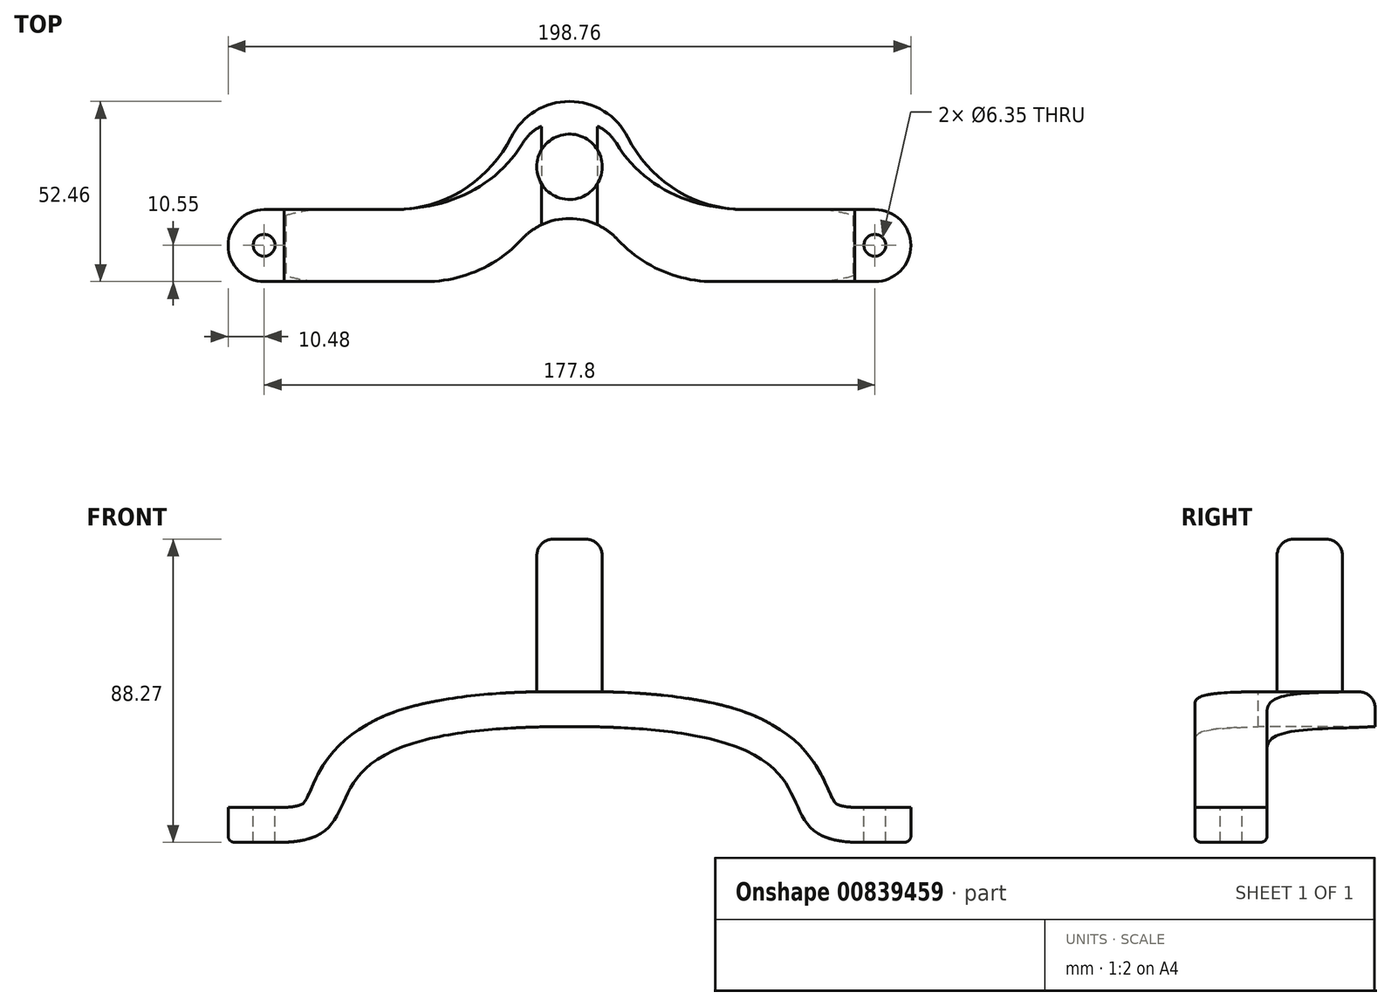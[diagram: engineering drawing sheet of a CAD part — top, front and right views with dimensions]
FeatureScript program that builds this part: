
annotation { "Feature Type Name" : "Feature", "Feature Type Description" : "" }
export const myFeature = defineFeature(function(context is Context, id is Id, definition is map)
    precondition{}
    {
        {
            var Q0;
            Q0=qCreatedBy(makeId("Top.planeOp"),FACE);
            var sketch = newSketch(context, id + "F0", { "sketchPlane" : qUnion([Q0])});
            skCircle(sketch, "E0", {"center": v(0, 0) * mm, "radius": 9.53 * mm});
            skSolve(sketch);
        }
        {
            var Q0;
            Q0=makeQuery(id+"F0.imprint","IMPRINT",FACE,{"disambiguationData":[TD([[makeQuery(id+"F0.imprint","IMPRINT",EDGE,{"derivedFrom":sQuery(id+"F0.wireOp",EDGE,"E0")}),1.0]])]});
            extrude(context, id + "F1", {"entities" : qUnion([Q0]), "depth" : 44.45 * mm, "offsetDistance" : 25.4 * mm});
        }
        {
            var Q0;
            Q0=qCreatedBy(makeId("Top.planeOp"),FACE);
            var sketch = newSketch(context, id + "F2", { "sketchPlane" : qUnion([Q0])});
            skLineSegment(sketch, "E1", {"start": v(0, 0) * mm, "end": v(0, -22.86) * mm, "construction": true});
            skLineSegment(sketch, "E2", {"start": v(0, -22.86) * mm, "end": v(88.9, -22.86) * mm, "construction": true});
            skLineSegment(sketch, "E3", {"start": v(0, -22.86) * mm, "end": v(-88.9, -22.86) * mm, "construction": true});
            skCircle(sketch, "E4", {"center": v(-88.9, -22.86) * mm, "radius": 3.18 * mm});
            skCircle(sketch, "E5", {"center": v(88.9, -22.86) * mm, "radius": 3.18 * mm});
            skSolve(sketch);
        }
        {
            var Q0;
            Q0=qCreatedBy(makeId("Top.planeOp"),FACE);
            var sketch = newSketch(context, id + "F3", { "sketchPlane" : qUnion([Q0])});
            skArc(sketch, "E6", {"start": v(14.41, -12.46) * mm, "mid": v(0, 19.05) * mm, "end": v(-14.41, -12.46) * mm});
            skLineSegment(sketch, "E7.bottom", {"start": v(88.9, -33.41) * mm, "end": v(-88.9, -33.41) * mm});
            skLineSegment(sketch, "E7.top", {"start": v(88.9, -12.46) * mm, "end": v(14.41, -12.46) * mm});
            skLineSegment(sketch, "E7.left", {"start": v(88.9, -33.41) * mm, "end": v(88.9, -12.46) * mm});
            skLineSegment(sketch, "E7.right", {"start": v(-88.9, -33.41) * mm, "end": v(-88.9, -12.46) * mm});
            skPoint(sketch, "E7.middle", {"position": v(0, -22.94) * mm});
            skLineSegment(sketch, "E8.trimOffspring", {"start": v(-14.41, -12.46) * mm, "end": v(-88.9, -12.46) * mm});
            skLineSegment(sketch, "E9", {"start": v(0, 0) * mm, "end": v(0, -22.94) * mm, "construction": true});
            skLineSegment(sketch, "E10", {"start": v(0, -22.94) * mm, "end": v(-88.9, -22.94) * mm, "construction": true});
            skLineSegment(sketch, "E11", {"start": v(0, -22.94) * mm, "end": v(88.9, -22.94) * mm, "construction": true});
            skCircle(sketch, "E12", {"center": v(-88.9, -22.94) * mm, "radius": 10.48 * mm});
            skCircle(sketch, "E13", {"center": v(88.9, -22.94) * mm, "radius": 10.48 * mm});
            skSolve(sketch);
        }
        {
            var Q0;
            Q0=makeQuery(id+"F3.imprint","IMPRINT",FACE,{"disambiguationData":[TD([[makeQuery(id+"F3.imprint","IMPRINT",EDGE,{"derivedFrom":sQuery(id+"F3.wireOp",EDGE,"E6")}),1.0]])]});
            var Q1;
            {var subQ0=sQuery(id+"F3.wireOp",EDGE,"E7.right");Q1=makeQuery(id+"F3.imprint","IMPRINT",FACE,{"disambiguationData":[TD([[makeQuery(id+"F3.imprint","IMPRINT",EDGE,{"derivedFrom":subQ0}),-1.0]])]});}
            var Q2;
            {var subQ0=sQuery(id+"F3.wireOp",EDGE,"E7.right");Q2=makeQuery(id+"F3.imprint","IMPRINT",FACE,{"disambiguationData":[TD([[makeQuery(id+"F3.imprint","IMPRINT",EDGE,{"derivedFrom":subQ0}),1.0]])]});}
            var Q3;
            {var subQ0=sQuery(id+"F3.wireOp",EDGE,"E7.left");Q3=makeQuery(id+"F3.imprint","IMPRINT",FACE,{"disambiguationData":[TD([[makeQuery(id+"F3.imprint","IMPRINT",EDGE,{"derivedFrom":subQ0}),1.0]])]});}
            var Q4;
            {var subQ0=sQuery(id+"F3.wireOp",EDGE,"E7.left");Q4=makeQuery(id+"F3.imprint","IMPRINT",FACE,{"disambiguationData":[TD([[makeQuery(id+"F3.imprint","IMPRINT",EDGE,{"derivedFrom":subQ0}),-1.0]])]});}
            extrude(context, id + "F4", {"entities" : qUnion([Q0, Q1, Q2, Q3, Q4]), "operationType" : NewBodyOperationType.ADD, "oppositeDirection" : true, "depth" : 43.81 * mm, "offsetDistance" : 25.4 * mm});
        }
        {
            var Q0;
            Q0=makeQuery(id+"F4.opExtrude","SWEPT_EDGE",EDGE,{"disambiguationData":[OSD([sQuery(id+"F3.wireOp",EDGE,"E6"),sQuery(id+"F3.wireOp",EDGE,"E7.top")])]});
            var Q1;
            Q1=makeQuery(id+"F4.opExtrude","SWEPT_EDGE",EDGE,{"disambiguationData":[OSD([sQuery(id+"F3.wireOp",EDGE,"E6"),sQuery(id+"F3.wireOp",EDGE,"E8.trimOffspring")])]});
            fillet(context, id + "F5", {"entities" : qUnion([Q0, Q1]), "radius" : 38.1 * mm, "tangentPropagation" : true, "allowEdgeOverflow" : false});
        }
        {
            var Q0;
            Q0=makeQuery(id+"F4.opExtrude","SWEPT_FACE",FACE,{"disambiguationData":[OSD([sQuery(id+"F3.wireOp",EDGE,"E7.bottom")])]});
            var sketch = newSketch(context, id + "F6", { "sketchPlane" : qUnion([Q0])});
            skLineSegment(sketch, "E14", {"start": v(0, -43.81) * mm, "end": v(-82.55, -43.82) * mm, "construction": true});
            skLineSegment(sketch, "E15", {"start": v(-83.03, -33.67) * mm, "end": v(-104.9, -33.67) * mm});
            skLineSegment(sketch, "E16", {"start": v(-104.9, -33.67) * mm, "end": v(-104.9, -43.82) * mm});
            skLineSegment(sketch, "E17", {"start": v(-104.9, -43.82) * mm, "end": v(-82.55, -43.82) * mm});
            skLineSegment(sketch, "E18", {"start": v(83.03, -33.67) * mm, "end": v(108.35, -33.67) * mm});
            skLineSegment(sketch, "E19", {"start": v(108.35, -33.67) * mm, "end": v(108.35, -43.82) * mm});
            skLineSegment(sketch, "E20", {"start": v(108.35, -43.82) * mm, "end": v(82.55, -43.82) * mm});
            skLineSegment(sketch, "E21", {"start": v(0, 0) * mm, "end": v(0, -10.16) * mm, "construction": true});
            skFitSpline(sketch, "E22", {"points": [v(-82.55, -43.82) * mm, v(0, -10.16) * mm], "startDerivative": vector(94.97, 4.46) * mm, "endDerivative": vector(266.7, -0.76) * mm});
            skFitSpline(sketch, "E23.MirrorCS", {"points": [v(82.55, -43.82) * mm, v(0, -10.16) * mm], "startDerivative": vector(-94.97, 4.46) * mm, "endDerivative": vector(-266.7, -0.76) * mm});
            skFitSpline(sketch, "E24.0", {"points": [v(-83.03, -33.67) * mm, v(-82.27, -33.63) * mm, v(-80.92, -33.52) * mm, v(-79.44, -33.26) * mm, v(-78.44, -32.98) * mm, v(-77.87, -32.74) * mm, v(-77.6, -32.58) * mm, v(-77.47, -32.48) * mm, v(-77.35, -32.36) * mm, v(-77.13, -32.1) * mm, v(-76.8, -31.6) * mm, v(-76.38, -30.8) * mm, v(-75.87, -29.71) * mm, v(-75.05, -27.88) * mm, v(-73.73, -24.94) * mm, v(-71.75, -21.4) * mm, v(-69.6, -18.44) * mm, v(-67.66, -16.22) * mm, v(-65.4, -14.07) * mm, v(-62.81, -12.02) * mm, v(-59.9, -10.12) * mm, v(-55.57, -7.8) * mm, v(-49.32, -5.32) * mm, v(-40.25, -2.98) * mm, v(-29.3, -1.27) * mm, v(-16.15, -0.21) * mm, v(-5.68, 0.02) * mm, v(0.03, 0) * mm]});
            skFitSpline(sketch, "E25.0", {"points": [v(83.03, -33.67) * mm, v(82.27, -33.63) * mm, v(80.92, -33.52) * mm, v(79.44, -33.26) * mm, v(78.44, -32.98) * mm, v(77.87, -32.74) * mm, v(77.6, -32.58) * mm, v(77.47, -32.48) * mm, v(77.35, -32.36) * mm, v(77.13, -32.1) * mm, v(76.8, -31.6) * mm, v(76.38, -30.8) * mm, v(75.87, -29.71) * mm, v(75.05, -27.88) * mm, v(73.73, -24.94) * mm, v(71.75, -21.4) * mm, v(69.6, -18.44) * mm, v(67.66, -16.22) * mm, v(65.4, -14.07) * mm, v(62.81, -12.02) * mm, v(59.9, -10.12) * mm, v(55.57, -7.8) * mm, v(49.32, -5.32) * mm, v(40.25, -2.98) * mm, v(29.3, -1.27) * mm, v(16.15, -0.21) * mm, v(5.68, 0.02) * mm, v(-0.03, 0) * mm]});
            skSolve(sketch);
        }
        {
            var Q0;
            Q0 = qSketchRegion(id + "F6", true);
            extrude(context, id + "F7", {"entities" : qUnion([Q0]), "operationType" : NewBodyOperationType.INTERSECT, "endBound" : BoundingType.THROUGH_ALL, "oppositeDirection" : true, "depth" : 25.4 * mm, "offsetDistance" : 25.4 * mm});
        }
        {
            var Q0;
            Q0 = qSketchRegion(id + "F0", true);
            extrude(context, id + "F8", {"entities" : qUnion([Q0]), "operationType" : NewBodyOperationType.ADD, "depth" : 44.45 * mm, "offsetDistance" : 25.4 * mm});
        }
        {
            var Q0;
            {var subQ0=sQuery(id+"F3.wireOp",EDGE,"E7.bottom");Q0=makeQuery(id+"F7.boolean.opBoolean","SPLIT",FACE,{"disambiguationData":[TD([makeQuery(id+"F4.opExtrude","SWEPT_FACE",FACE,{"disambiguationData":[OSD([subQ0])]})])],"derivedFrom":makeQuery(id+"F4.opExtrude","CAP_FACE",FACE,{"disambiguationData":[OSD([sQuery(id+"F3.wireOp",EDGE,"E6"),subQ0,sQuery(id+"F3.wireOp",EDGE,"E7.top"),sQuery(id+"F3.wireOp",EDGE,"E8.trimOffspring"),sQuery(id+"F3.wireOp",EDGE,"E12"),sQuery(id+"F3.wireOp",EDGE,"E13")])],"isStart":true})});}
            var sketch = newSketch(context, id + "F9", { "sketchPlane" : qUnion([Q0])});
            skCircle(sketch, "E26", {"center": v(0, -34.1) * mm, "radius": 19.05 * mm});
            skSolve(sketch);
        }
        {
            var Q0;
            {var subQ1=sQuery(id+"F3.wireOp",EDGE,"E7.bottom");var subQ7=makeQuery(id+"F4.opExtrude","CAP_EDGE",EDGE,{"disambiguationData":[OSD([subQ1])],"isStart":true});Q0=makeQuery(id+"F9.imprint","IMPRINT",FACE,{"disambiguationData":[TD([[makeQuery(id+"F9.imprint","IMPRINT",EDGE,{"derivedFrom":subQ7}),-1.0]])]});}
            var Q1;
            {var subQ1=sQuery(id+"F3.wireOp",EDGE,"E7.bottom");var subQ7=makeQuery(id+"F4.opExtrude","CAP_EDGE",EDGE,{"disambiguationData":[OSD([subQ1])],"isStart":true});Q1=makeQuery(id+"F9.imprint","IMPRINT",FACE,{"disambiguationData":[TD([[makeQuery(id+"F9.imprint","IMPRINT",EDGE,{"derivedFrom":subQ7}),1.0]])]});}
            extrude(context, id + "F10", {"entities" : qUnion([Q0, Q1]), "operationType" : NewBodyOperationType.REMOVE, "endBound" : BoundingType.THROUGH_ALL, "oppositeDirection" : true, "depth" : 25.4 * mm, "offsetDistance" : 25.4 * mm});
        }
        {
            var Q0;
            Q0=makeQuery(id+"F10.boolean.opBoolean","INTERSECT",EDGE,{"disambiguationData":[OD(0.0)],"derivedFrom":[makeQuery(id+"F4.opExtrude","SWEPT_FACE",FACE,{"disambiguationData":[OSD([sQuery(id+"F3.wireOp",EDGE,"E7.bottom")])]}),makeQuery(id+"F10.opExtrude","SWEPT_FACE",FACE,{"disambiguationData":[OSD([sQuery(id+"F9.wireOp",EDGE,"E26")])]})]});
            var Q1;
            Q1=makeQuery(id+"F10.boolean.opBoolean","INTERSECT",EDGE,{"disambiguationData":[OD(1.0)],"derivedFrom":[makeQuery(id+"F4.opExtrude","SWEPT_FACE",FACE,{"disambiguationData":[OSD([sQuery(id+"F3.wireOp",EDGE,"E7.bottom")])]}),makeQuery(id+"F10.opExtrude","SWEPT_FACE",FACE,{"disambiguationData":[OSD([sQuery(id+"F9.wireOp",EDGE,"E26")])]})]});
            fillet(context, id + "F11", {"entities" : qUnion([Q0, Q1]), "radius" : 38.1 * mm, "tangentPropagation" : true, "allowEdgeOverflow" : false});
        }
        {
            var Q0;
            Q0=makeQuery(id+"F4.opExtrude","CAP_EDGE",EDGE,{"disambiguationData":[OSD([sQuery(id+"F3.wireOp",EDGE,"E6")])],"isStart":true});
            var Q1;
            Q1=makeQuery(id+"F7.boolean.opBoolean","INTERSECT",EDGE,{"derivedFrom":[makeQuery(id+"F4.opExtrude","SWEPT_FACE",FACE,{"disambiguationData":[OSD([sQuery(id+"F3.wireOp",EDGE,"E6")])]}),makeQuery(id+"F7.boolean.toolComplement.opBoolean","COPY",FACE,{"derivedFrom":makeQuery(id+"F7.opExtrude","SWEPT_FACE",FACE,{"disambiguationData":[OSD([sQuery(id+"F6.wireOp",EDGE,"a3f56aa1-5c8b-43e5-82c6-7868b8ca9d38.0")])]})})]});
            var Q2;
            Q2=makeQuery(id+"F7.boolean.opBoolean","INTERSECT",EDGE,{"derivedFrom":[makeQuery(id+"F5.opFillet","BLEND_FACE",FACE,{"disambiguationData":[OSD([sQuery(id+"F3.wireOp",EDGE,"E6"),sQuery(id+"F3.wireOp",EDGE,"E7.top")])]}),makeQuery(id+"F7.boolean.toolComplement.opBoolean","COPY",FACE,{"derivedFrom":makeQuery(id+"F7.opExtrude","SWEPT_FACE",FACE,{"disambiguationData":[OSD([sQuery(id+"F6.wireOp",EDGE,"2b992f9c-3d7e-4ba6-b69b-49b9b1f304800.MirrorCS")])]})})]});
            var Q3;
            Q3=makeQuery(id+"F7.boolean.opBoolean","INTERSECT",EDGE,{"derivedFrom":[makeQuery(id+"F4.opExtrude","SWEPT_FACE",FACE,{"disambiguationData":[OSD([sQuery(id+"F3.wireOp",EDGE,"E6")])]}),makeQuery(id+"F7.boolean.toolComplement.opBoolean","COPY",FACE,{"derivedFrom":makeQuery(id+"F7.opExtrude","SWEPT_FACE",FACE,{"disambiguationData":[OSD([sQuery(id+"F6.wireOp",EDGE,"2b992f9c-3d7e-4ba6-b69b-49b9b1f304800.MirrorCS")])]})})]});
            var Q4;
            Q4=makeQuery(id+"F7.boolean.opBoolean","INTERSECT",EDGE,{"derivedFrom":[makeQuery(id+"F4.opExtrude","SWEPT_FACE",FACE,{"disambiguationData":[OSD([sQuery(id+"F3.wireOp",EDGE,"E6")])]}),makeQuery(id+"F7.boolean.toolComplement.opBoolean","COPY",FACE,{"derivedFrom":makeQuery(id+"F7.opExtrude","SWEPT_FACE",FACE,{"disambiguationData":[OSD([sQuery(id+"F6.wireOp",EDGE,"f722ad29-e965-4c17-baed-5adea42b7f95")])]})})]});
            var Q5;
            Q5=makeQuery(id+"F7.boolean.opBoolean","INTERSECT",EDGE,{"derivedFrom":[makeQuery(id+"F5.opFillet","BLEND_FACE",FACE,{"disambiguationData":[OSD([sQuery(id+"F3.wireOp",EDGE,"E6"),sQuery(id+"F3.wireOp",EDGE,"E8.trimOffspring")])]}),makeQuery(id+"F7.boolean.toolComplement.opBoolean","COPY",FACE,{"derivedFrom":makeQuery(id+"F7.opExtrude","SWEPT_FACE",FACE,{"disambiguationData":[OSD([sQuery(id+"F6.wireOp",EDGE,"f722ad29-e965-4c17-baed-5adea42b7f95")])]})})]});
            var Q6;
            Q6=makeQuery(id+"F7.boolean.opBoolean","INTERSECT",EDGE,{"derivedFrom":[makeQuery(id+"F4.opExtrude","SWEPT_FACE",FACE,{"disambiguationData":[OSD([sQuery(id+"F3.wireOp",EDGE,"E8.trimOffspring")])]}),makeQuery(id+"F7.boolean.toolComplement.opBoolean","COPY",FACE,{"derivedFrom":makeQuery(id+"F7.opExtrude","SWEPT_FACE",FACE,{"disambiguationData":[OSD([sQuery(id+"F6.wireOp",EDGE,"f722ad29-e965-4c17-baed-5adea42b7f95")])]})})]});
            var Q7;
            Q7=makeQuery(id+"F7.boolean.opBoolean","INTERSECT",EDGE,{"derivedFrom":[makeQuery(id+"F4.opExtrude","SWEPT_FACE",FACE,{"disambiguationData":[OSD([sQuery(id+"F3.wireOp",EDGE,"E8.trimOffspring")])]}),makeQuery(id+"F7.boolean.toolComplement.opBoolean","COPY",FACE,{"derivedFrom":makeQuery(id+"F7.opExtrude","SWEPT_FACE",FACE,{"disambiguationData":[OSD([sQuery(id+"F6.wireOp",EDGE,"0e30f15a-034d-4650-8b6f-ae2eca744b7f.0")])]})})]});
            var Q8;
            Q8=makeQuery(id+"F7.boolean.opBoolean","INTERSECT",EDGE,{"derivedFrom":[makeQuery(id+"F5.opFillet","BLEND_FACE",FACE,{"disambiguationData":[OSD([sQuery(id+"F3.wireOp",EDGE,"E6"),sQuery(id+"F3.wireOp",EDGE,"E8.trimOffspring")])]}),makeQuery(id+"F7.boolean.toolComplement.opBoolean","COPY",FACE,{"derivedFrom":makeQuery(id+"F7.opExtrude","SWEPT_FACE",FACE,{"disambiguationData":[OSD([sQuery(id+"F6.wireOp",EDGE,"0e30f15a-034d-4650-8b6f-ae2eca744b7f.0")])]})})]});
            var Q9;
            Q9=makeQuery(id+"F7.boolean.opBoolean","INTERSECT",EDGE,{"derivedFrom":[makeQuery(id+"F4.opExtrude","SWEPT_FACE",FACE,{"disambiguationData":[OSD([sQuery(id+"F3.wireOp",EDGE,"E6")])]}),makeQuery(id+"F7.boolean.toolComplement.opBoolean","COPY",FACE,{"derivedFrom":makeQuery(id+"F7.opExtrude","SWEPT_FACE",FACE,{"disambiguationData":[OSD([sQuery(id+"F6.wireOp",EDGE,"0e30f15a-034d-4650-8b6f-ae2eca744b7f.0")])]})})]});
            var Q10;
            Q10=makeQuery(id+"F7.boolean.opBoolean","INTERSECT",EDGE,{"derivedFrom":[makeQuery(id+"F5.opFillet","BLEND_FACE",FACE,{"disambiguationData":[OSD([sQuery(id+"F3.wireOp",EDGE,"E6"),sQuery(id+"F3.wireOp",EDGE,"E7.top")])]}),makeQuery(id+"F7.boolean.toolComplement.opBoolean","COPY",FACE,{"derivedFrom":makeQuery(id+"F7.opExtrude","SWEPT_FACE",FACE,{"disambiguationData":[OSD([sQuery(id+"F6.wireOp",EDGE,"a3f56aa1-5c8b-43e5-82c6-7868b8ca9d38.0")])]})})]});
            var Q11;
            Q11=makeQuery(id+"F7.boolean.opBoolean","INTERSECT",EDGE,{"derivedFrom":[makeQuery(id+"F4.opExtrude","SWEPT_FACE",FACE,{"disambiguationData":[OSD([sQuery(id+"F3.wireOp",EDGE,"E7.top")])]}),makeQuery(id+"F7.boolean.toolComplement.opBoolean","COPY",FACE,{"derivedFrom":makeQuery(id+"F7.opExtrude","SWEPT_FACE",FACE,{"disambiguationData":[OSD([sQuery(id+"F6.wireOp",EDGE,"2b992f9c-3d7e-4ba6-b69b-49b9b1f304800.MirrorCS")])]})})]});
            var Q12;
            Q12=makeQuery(id+"F7.boolean.opBoolean","COPY",EDGE,{"derivedFrom":makeQuery(id+"F7.boolean.toolComplement.opBoolean","COPY",EDGE,{"derivedFrom":makeQuery(id+"F7.opExtrude","CAP_EDGE",EDGE,{"disambiguationData":[OSD([sQuery(id+"F6.wireOp",EDGE,"0e30f15a-034d-4650-8b6f-ae2eca744b7f.0")])],"isStart":true})})});
            var Q13;
            Q13=makeQuery(id+"F11.opFillet","BLEND_EDGE",EDGE,{"blendedFrom":[makeQuery(id+"F10.boolean.opBoolean","INTERSECT",EDGE,{"disambiguationData":[OD(0.0)],"derivedFrom":[makeQuery(id+"F4.opExtrude","SWEPT_FACE",FACE,{"disambiguationData":[OSD([sQuery(id+"F3.wireOp",EDGE,"E7.bottom")])]}),makeQuery(id+"F10.opExtrude","SWEPT_FACE",FACE,{"disambiguationData":[OSD([sQuery(id+"F9.wireOp",EDGE,"E26")])]})]}),makeQuery(id+"F7.boolean.opBoolean","COPY",FACE,{"derivedFrom":makeQuery(id+"F7.boolean.toolComplement.opBoolean","COPY",FACE,{"derivedFrom":makeQuery(id+"F7.opExtrude","SWEPT_FACE",FACE,{"disambiguationData":[OSD([sQuery(id+"F6.wireOp",EDGE,"0e30f15a-034d-4650-8b6f-ae2eca744b7f.0")])]})})})],"blendedInto":[makeQuery(id+"F7.boolean.opBoolean","COPY",FACE,{"derivedFrom":makeQuery(id+"F7.boolean.toolComplement.opBoolean","COPY",FACE,{"derivedFrom":makeQuery(id+"F7.opExtrude","SWEPT_FACE",FACE,{"disambiguationData":[OSD([sQuery(id+"F6.wireOp",EDGE,"0e30f15a-034d-4650-8b6f-ae2eca744b7f.0")])]})})})]});
            var Q14;
            Q14=makeQuery(id+"F11.opFillet","BLEND_EDGE",EDGE,{"blendedFrom":[makeQuery(id+"F10.boolean.opBoolean","INTERSECT",EDGE,{"disambiguationData":[OD(0.0)],"derivedFrom":[makeQuery(id+"F4.opExtrude","SWEPT_FACE",FACE,{"disambiguationData":[OSD([sQuery(id+"F3.wireOp",EDGE,"E7.bottom")])]}),makeQuery(id+"F10.opExtrude","SWEPT_FACE",FACE,{"disambiguationData":[OSD([sQuery(id+"F9.wireOp",EDGE,"E26")])]})]}),makeQuery(id+"F7.boolean.opBoolean","COPY",FACE,{"derivedFrom":makeQuery(id+"F7.boolean.toolComplement.opBoolean","COPY",FACE,{"derivedFrom":makeQuery(id+"F7.opExtrude","SWEPT_FACE",FACE,{"disambiguationData":[OSD([sQuery(id+"F6.wireOp",EDGE,"f722ad29-e965-4c17-baed-5adea42b7f95")])]})})})],"blendedInto":[makeQuery(id+"F7.boolean.opBoolean","COPY",FACE,{"derivedFrom":makeQuery(id+"F7.boolean.toolComplement.opBoolean","COPY",FACE,{"derivedFrom":makeQuery(id+"F7.opExtrude","SWEPT_FACE",FACE,{"disambiguationData":[OSD([sQuery(id+"F6.wireOp",EDGE,"f722ad29-e965-4c17-baed-5adea42b7f95")])]})})})]});
            var Q15;
            Q15=makeQuery(id+"F7.boolean.opBoolean","COPY",EDGE,{"derivedFrom":makeQuery(id+"F7.boolean.toolComplement.opBoolean","COPY",EDGE,{"derivedFrom":makeQuery(id+"F7.opExtrude","CAP_EDGE",EDGE,{"disambiguationData":[OSD([sQuery(id+"F6.wireOp",EDGE,"f722ad29-e965-4c17-baed-5adea42b7f95")])],"isStart":true})})});
            var Q16;
            Q16=makeQuery(id+"F10.boolean.opBoolean","INTERSECT",EDGE,{"derivedFrom":[makeQuery(id+"F7.boolean.opBoolean","COPY",FACE,{"derivedFrom":makeQuery(id+"F7.boolean.toolComplement.opBoolean","COPY",FACE,{"derivedFrom":makeQuery(id+"F7.opExtrude","SWEPT_FACE",FACE,{"disambiguationData":[OSD([sQuery(id+"F6.wireOp",EDGE,"0e30f15a-034d-4650-8b6f-ae2eca744b7f.0")])]})})}),makeQuery(id+"F10.opExtrude","SWEPT_FACE",FACE,{"disambiguationData":[OSD([sQuery(id+"F9.wireOp",EDGE,"E26")])]})]});
            var Q17;
            Q17=makeQuery(id+"F10.boolean.opBoolean","COPY",EDGE,{"derivedFrom":makeQuery(id+"F10.opExtrude","CAP_EDGE",EDGE,{"disambiguationData":[OSD([sQuery(id+"F9.wireOp",EDGE,"E26")])],"isStart":true})});
            var Q18;
            Q18=makeQuery(id+"F10.boolean.opBoolean","INTERSECT",EDGE,{"derivedFrom":[makeQuery(id+"F7.boolean.opBoolean","COPY",FACE,{"derivedFrom":makeQuery(id+"F7.boolean.toolComplement.opBoolean","COPY",FACE,{"derivedFrom":makeQuery(id+"F7.opExtrude","SWEPT_FACE",FACE,{"disambiguationData":[OSD([sQuery(id+"F6.wireOp",EDGE,"f722ad29-e965-4c17-baed-5adea42b7f95")])]})})}),makeQuery(id+"F10.opExtrude","SWEPT_FACE",FACE,{"disambiguationData":[OSD([sQuery(id+"F9.wireOp",EDGE,"E26")])]})]});
            var Q19;
            Q19=makeQuery(id+"F11.opFillet","BLEND_EDGE",EDGE,{"blendedFrom":[makeQuery(id+"F10.boolean.opBoolean","INTERSECT",EDGE,{"disambiguationData":[OD(1.0)],"derivedFrom":[makeQuery(id+"F4.opExtrude","SWEPT_FACE",FACE,{"disambiguationData":[OSD([sQuery(id+"F3.wireOp",EDGE,"E7.bottom")])]}),makeQuery(id+"F10.opExtrude","SWEPT_FACE",FACE,{"disambiguationData":[OSD([sQuery(id+"F9.wireOp",EDGE,"E26")])]})]}),makeQuery(id+"F7.boolean.opBoolean","COPY",FACE,{"derivedFrom":makeQuery(id+"F7.boolean.toolComplement.opBoolean","COPY",FACE,{"derivedFrom":makeQuery(id+"F7.opExtrude","SWEPT_FACE",FACE,{"disambiguationData":[OSD([sQuery(id+"F6.wireOp",EDGE,"a3f56aa1-5c8b-43e5-82c6-7868b8ca9d38.0")])]})})})],"blendedInto":[makeQuery(id+"F7.boolean.opBoolean","COPY",FACE,{"derivedFrom":makeQuery(id+"F7.boolean.toolComplement.opBoolean","COPY",FACE,{"derivedFrom":makeQuery(id+"F7.opExtrude","SWEPT_FACE",FACE,{"disambiguationData":[OSD([sQuery(id+"F6.wireOp",EDGE,"a3f56aa1-5c8b-43e5-82c6-7868b8ca9d38.0")])]})})})]});
            var Q20;
            Q20=makeQuery(id+"F11.opFillet","BLEND_EDGE",EDGE,{"blendedFrom":[makeQuery(id+"F10.boolean.opBoolean","INTERSECT",EDGE,{"disambiguationData":[OD(1.0)],"derivedFrom":[makeQuery(id+"F4.opExtrude","SWEPT_FACE",FACE,{"disambiguationData":[OSD([sQuery(id+"F3.wireOp",EDGE,"E7.bottom")])]}),makeQuery(id+"F10.opExtrude","SWEPT_FACE",FACE,{"disambiguationData":[OSD([sQuery(id+"F9.wireOp",EDGE,"E26")])]})]}),makeQuery(id+"F7.boolean.opBoolean","COPY",FACE,{"derivedFrom":makeQuery(id+"F7.boolean.toolComplement.opBoolean","COPY",FACE,{"derivedFrom":makeQuery(id+"F7.opExtrude","SWEPT_FACE",FACE,{"disambiguationData":[OSD([sQuery(id+"F6.wireOp",EDGE,"2b992f9c-3d7e-4ba6-b69b-49b9b1f304800.MirrorCS")])]})})})],"blendedInto":[makeQuery(id+"F7.boolean.opBoolean","COPY",FACE,{"derivedFrom":makeQuery(id+"F7.boolean.toolComplement.opBoolean","COPY",FACE,{"derivedFrom":makeQuery(id+"F7.opExtrude","SWEPT_FACE",FACE,{"disambiguationData":[OSD([sQuery(id+"F6.wireOp",EDGE,"2b992f9c-3d7e-4ba6-b69b-49b9b1f304800.MirrorCS")])]})})})]});
            var Q21;
            Q21=makeQuery(id+"F8.opExtrude","CAP_EDGE",EDGE,{"disambiguationData":[OSD([sQuery(id+"F0.wireOp",EDGE,"E0")])],"isStart":false});
            fillet(context, id + "F12", {"entities" : qUnion([Q0, Q1, Q2, Q3, Q4, Q5, Q6, Q7, Q8, Q9, Q10, Q11, Q12, Q13, Q14, Q15, Q16, Q17, Q18, Q19, Q20, Q21]), "radius" : 4.83 * mm, "tangentPropagation" : true, "allowEdgeOverflow" : false});
        }
        {
            var Q0;
            Q0=makeQuery(id+"F7.boolean.opBoolean","INTERSECT",EDGE,{"derivedFrom":[makeQuery(id+"F4.opExtrude","SWEPT_FACE",FACE,{"disambiguationData":[OSD([sQuery(id+"F3.wireOp",EDGE,"E12")])]}),makeQuery(id+"F7.boolean.toolComplement.opBoolean","COPY",FACE,{"derivedFrom":makeQuery(id+"F7.opExtrude","SWEPT_FACE",FACE,{"disambiguationData":[OSD([sQuery(id+"F6.wireOp",EDGE,"E15")])]})})]});
            var Q1;
            Q1=makeQuery(id+"F7.boolean.opBoolean","INTERSECT",EDGE,{"derivedFrom":[makeQuery(id+"F4.opExtrude","SWEPT_FACE",FACE,{"disambiguationData":[OSD([sQuery(id+"F3.wireOp",EDGE,"E13")])]}),makeQuery(id+"F7.boolean.toolComplement.opBoolean","COPY",FACE,{"derivedFrom":makeQuery(id+"F7.opExtrude","SWEPT_FACE",FACE,{"disambiguationData":[OSD([sQuery(id+"F6.wireOp",EDGE,"E18")])]})})]});
            var Q2;
            Q2=makeQuery(id+"F4.opExtrude","CAP_EDGE",EDGE,{"disambiguationData":[OSD([sQuery(id+"F3.wireOp",EDGE,"E12")])],"isStart":false});
            var Q3;
            Q3=makeQuery(id+"F4.opExtrude","CAP_EDGE",EDGE,{"disambiguationData":[OSD([sQuery(id+"F3.wireOp",EDGE,"E13")])],"isStart":false});
            fillet(context, id + "F13", {"entities" : qUnion([Q0, Q1, Q2, Q3]), "radius" : 1.78 * mm, "tangentPropagation" : true, "allowEdgeOverflow" : false});
        }
        {
            var Q0;
            Q0 = qSketchRegion(id + "F2", true);
            extrude(context, id + "F14", {"entities" : qUnion([Q0]), "operationType" : NewBodyOperationType.REMOVE, "endBound" : BoundingType.THROUGH_ALL, "oppositeDirection" : true, "depth" : 25.4 * mm, "offsetDistance" : 25.4 * mm});
        }
        {
            var Q0;
            Q0=qCreatedBy(makeId("Top.planeOp"),FACE);
            cPlane(context, id + "F15", {"entities" : qUnion([Q0]), "cplaneType" : CPlaneType.OFFSET, "offset" : 12.7 * mm, "oppositeDirection" : true, "width" : 152.4 * mm, "height" : 152.4 * mm});
        }
    });
